FCSTD DOCUMENT  (FreeCAD 0.19R)
Label: jacquard_module_3
License: All rights reserved
LicenseURL: http://en.wikipedia.org/wiki/All_rights_reserved
objects: Sketcher::SketchObject×1, PartDesign::Body×1, Spreadsheet::Sheet×1
note: 2 computed .brp shape members not serialized (recipe doc carries the construction recipe); baked Part::Feature solids carry a one-line shape summary decoded from their .brp

FEATURE [Sketcher::SketchObject] Sketch
  FullyConstrained = true
  MapMode = 5
  Support = -> [XY_Plane]
  expr: Constraints[55] = 2mm + 2mm * <<Params>>.DropSequence
  expr: Constraints[51] = 10mm + 10mm * <<Params>>.RiseGroup
  expr: Constraints[56] = <<Params>>.RiseHeight
  sketch-geometry (21):
    g0: LineSegment StartX=0 StartY=30 StartZ=0 EndX=150 EndY=30 EndZ=0
    g1: LineSegment StartX=150 StartY=30 StartZ=0 EndX=160 EndY=40 EndZ=0
    g2: LineSegment StartX=160 StartY=40 StartZ=0 EndX=185 EndY=40 EndZ=0
    g3: LineSegment StartX=185 StartY=40 StartZ=0 EndX=185 EndY=55 EndZ=0
    g4: LineSegment StartX=185 StartY=55 StartZ=0 EndX=190 EndY=55 EndZ=0
    g5: LineSegment StartX=190 StartY=55 StartZ=0 EndX=190 EndY=40 EndZ=0
    g6: LineSegment StartX=190 StartY=40 StartZ=0 EndX=195 EndY=40 EndZ=0
    g7: LineSegment StartX=195 StartY=40 StartZ=0 EndX=195 EndY=55 EndZ=0
    g8: LineSegment StartX=195 StartY=55 StartZ=0 EndX=200 EndY=55 EndZ=0
    g9: LineSegment StartX=200 StartY=55 StartZ=0 EndX=200 EndY=0 EndZ=0
    g10: LineSegment StartX=200 StartY=0 StartZ=0 EndX=198 EndY=0 EndZ=0
    g11: LineSegment StartX=198 StartY=0 StartZ=0 EndX=183 EndY=-15 EndZ=0
    g12: LineSegment StartX=108 StartY=0 StartZ=0 EndX=0 EndY=0 EndZ=0
    g13: LineSegment StartX=0 StartY=0 StartZ=0 EndX=0 EndY=30 EndZ=0
    g14: Circle CenterX=10 CenterY=20 CenterZ=0 NormalX=0 NormalY=0 NormalZ=1 AngleXU=0 Radius=1.985
    g15: LineSegment StartX=183 StartY=-15 StartZ=0 EndX=128 EndY=-15 EndZ=0
    g16: LineSegment StartX=128 StartY=-15 StartZ=0 EndX=128 EndY=0 EndZ=0
    g17: LineSegment StartX=128 StartY=0 StartZ=0 EndX=118 EndY=0 EndZ=0
    g18: LineSegment StartX=118 StartY=0 StartZ=0 EndX=118 EndY=-15 EndZ=0
    g19: LineSegment StartX=118 StartY=-15 StartZ=0 EndX=108 EndY=-15 EndZ=0
    g20: LineSegment StartX=108 StartY=-15 StartZ=0 EndX=108 EndY=0 EndZ=0
  constraints (57):
    c: Coincident(g0,g1)
    c: Coincident(g1,g2)
    c: Horizontal(g2)
    c: Coincident(g2,g3)
    c: Coincident(g3,g4)
    c: Coincident(g4,g5)
    c: Coincident(g5,g6)
    c: Coincident(g6,g7)
    c: Vertical(g7)
    c: Coincident(g7,g8)
    c: Horizontal(g8)
    c: Coincident(g8,g9)
    c: Vertical(g9)
    c: Coincident(g9,g10)
    c: Coincident(g12,g13)
    c: Coincident(g13,g0)
    c: Vertical(g13)
    c: Horizontal(g0)
    c: Horizontal(g12)
    c: Vertical(g3)
    c: Vertical(g5)
    c: Tangent(g2,g6)
    c: Tangent(g8,g4)
    c: Angle(g1) = 0.785398
    c: DistanceX(g4,g4) = 5
    c: DistanceX(g8,g8) = 5
    c: DistanceX(g6,g6) = 5
    c: DistanceY(g3,g3) = 15
    c: DistanceY(g0,g1) = 10
    c: Distance(g14,g0) = 10
    c: Distance(g13) = 30
    c: Coincident(g11,g10)
    c: Angle(g11) = -2.35619
    c: Coincident(g15,g11)
    c: Horizontal(g15)
    c: Coincident(g16,g15)
    c: Coincident(g17,g16)
    c: Coincident(g18,g17)
    c: Vertical(g18)
    c: Coincident(g19,g18)
    c: Coincident(g20,g19)
    c: Coincident(g12,g20)
    c: Vertical(g20)
    c: Vertical(g16)
    c: Tangent(g17,g12)
    c: Tangent(g19,g15)
    c: Tangent(g10,g17)
    c: DistanceX(g15,g9) = 72
    c: DistanceX(g19,g19) = 10
    c: DistanceX(g12,g9) = 200
    c: DistanceX(g0,g0) = 150
    c: DistanceX(g17,g17) = 10
    c: Coincident(g12,g-1)
    c: DistanceX(g0,g14) = 10
    c: Diameter(g14) = 3.97
    c: DistanceX(g10,g10) = 2
    c: DistanceY(g19,g12) = 15
FEATURE [PartDesign::Body] Body
  Group = -> [Sketch]
  Origin = -> Origin
FEATURE [Spreadsheet::Sheet] Spreadsheet  label="Params"
  cells = A1=RiseHeight; B1(RiseHeight)==15mm; A2=RiseGroup; B2(RiseGroup)==B3 % 4; A3=DropSequence; B3(DropSequence)=0
